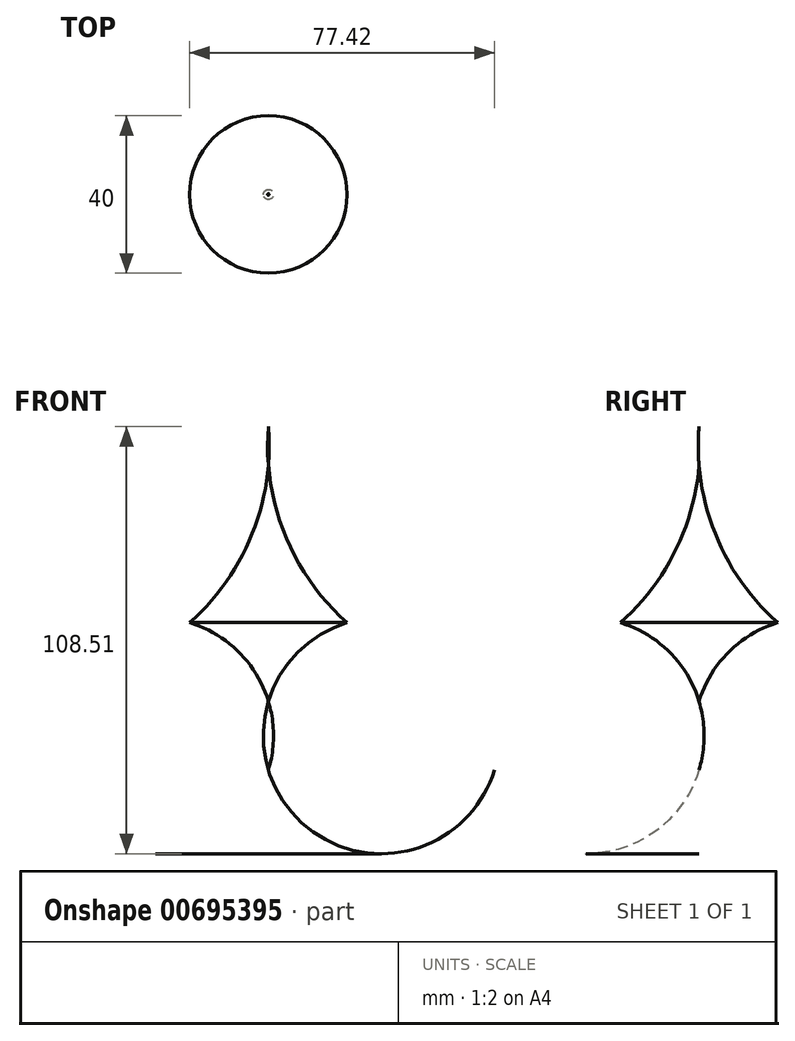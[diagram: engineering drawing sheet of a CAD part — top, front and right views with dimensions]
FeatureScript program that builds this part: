
annotation { "Feature Type Name" : "Feature", "Feature Type Description" : "" }
export const myFeature = defineFeature(function(context is Context, id is Id, definition is map)
    precondition{}
    {
        {
            var Q0;
            Q0=qCreatedBy(makeId("Right.planeOp"),FACE);
            var sketch = newSketch(context, id + "F0", { "sketchPlane" : qUnion([Q0])});
            skLineSegment(sketch, "E0", {"start": v(0, -37.92) * mm, "end": v(0, 69.63) * mm, "construction": true});
            skArc(sketch, "E1", {"start": v(20, 20) * mm, "mid": v(7.5, 12.5) * mm, "end": v(0, 0) * mm});
            skArc(sketch, "E2", {"start": v(0, 60) * mm, "mid": v(6.13, 38.07) * mm, "end": v(20, 20) * mm});
            skLineSegment(sketch, "E3", {"start": v(0, 60) * mm, "end": v(0, 0) * mm});
            skSolve(sketch);
        }
        {
            var Q0;
            Q0=makeQuery(id+"F0.imprint","IMPRINT",FACE,{"disambiguationData":[TD([[makeQuery(id+"F0.imprint","IMPRINT",EDGE,{"derivedFrom":sQuery(id+"F0.wireOp",EDGE,"E1")}),-1.0]])]});
            var Q1;
            Q1=sQuery(id+"F0.wireOp",EDGE,"E3");
            revolve(context, id + "F1", {"surfaceOperationType" : NewSurfaceOperationType.NEW, "entities" : qUnion([Q0]), "axis" : qUnion([Q1]), "revolveType" : RevolveType.FULL});
        }
    });
